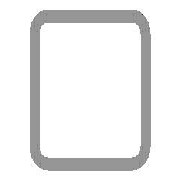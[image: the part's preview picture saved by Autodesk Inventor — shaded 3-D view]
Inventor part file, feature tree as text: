
AUTODESK INVENTOR PART (.ipt)
format: ipt  version: 2025 (Build 290162010, 162A)  size: 135,680 bytes
history: native  units: mm (DEFAULTED — no unit token found)
features: other x4, sketch x1, plane x1
ambient origin geometry x8: Origin, YZ Plane, XZ Plane, XY Plane, X Axis, Y Axis, Z Axis, Center Point
bodies: Solid1 (feature_tree), Body (feature_tree)
feature tree (6):
  parser-record x1  (decoder bookkeeping rows leaked as tree rows — omitted from the tree; the rows remain in map.json)
  other  "Driven Length"
  other  "Start plane"
  other  "End plane"
  sketch  "Sketch3"  dims[d3=5400.0mm d4=0.0mm d7=6.0mm d9=80.0mm d11=80.0mm d12=3.0mm d13=-0.0mm d14=5400.0mm d15=40.0mm d16=40.0mm d17=90.0deg d18=5400.0mm]
  plane  "Work Plane3"
